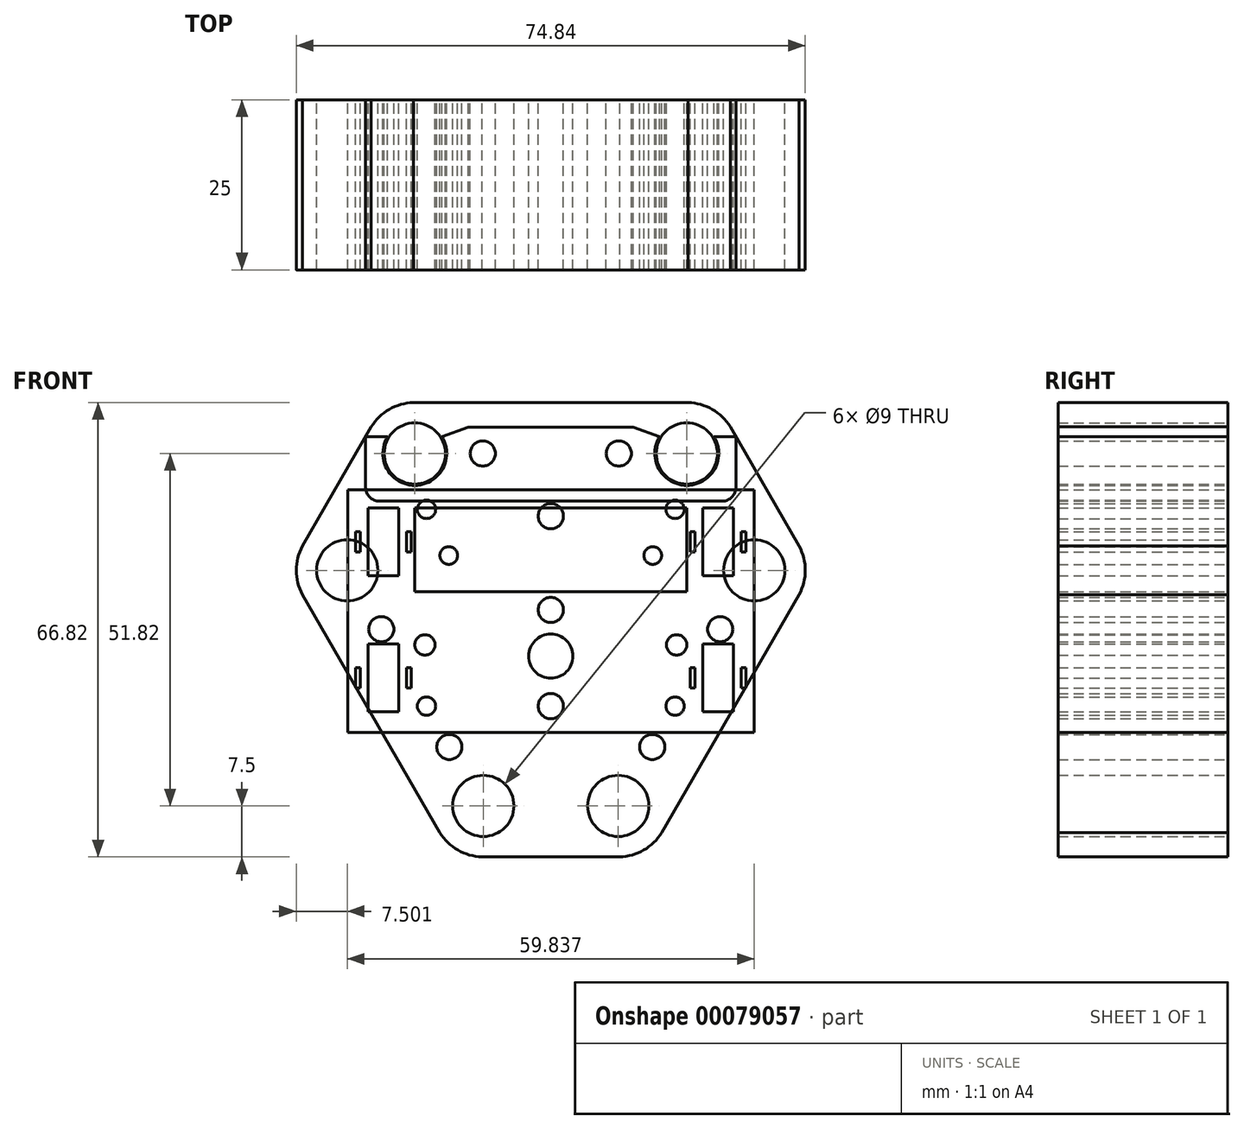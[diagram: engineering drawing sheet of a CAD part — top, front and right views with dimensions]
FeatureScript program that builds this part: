
annotation { "Feature Type Name" : "Feature", "Feature Type Description" : "" }
export const myFeature = defineFeature(function(context is Context, id is Id, definition is map)
    precondition{}
    {
        {
            var Q0;
            Q0=qCreatedBy(makeId("Front.planeOp"),FACE);
            var sketch = newSketch(context, id + "F0", { "sketchPlane" : qUnion([Q0])});
            skLineSegment(sketch, "E0.bottom", {"start": v(29.88, 17.64) * mm, "end": v(-29.88, 17.64) * mm});
            skLineSegment(sketch, "E0.left", {"start": v(29.88, 17.64) * mm, "end": v(29.88, -18) * mm});
            skLineSegment(sketch, "E0.right", {"start": v(-29.88, 17.64) * mm, "end": v(-29.88, -18) * mm});
            skPoint(sketch, "E0.middle", {"position": v(0, 0) * mm});
            skLineSegment(sketch, "E1.bottom", {"start": v(-22.38, 15) * mm, "end": v(-26.88, 15) * mm});
            skLineSegment(sketch, "E1.top", {"start": v(-22.38, 5) * mm, "end": v(-26.88, 5) * mm});
            skLineSegment(sketch, "E1.left", {"start": v(-22.38, 15) * mm, "end": v(-22.38, 5) * mm});
            skLineSegment(sketch, "E1.right", {"start": v(-26.88, 15) * mm, "end": v(-26.88, 5) * mm});
            skPoint(sketch, "E1.middle", {"position": v(-24.63, 10) * mm});
            skLineSegment(sketch, "E2", {"start": v(0, 17.64) * mm, "end": v(0, -17.64) * mm, "construction": true});
            skLineSegment(sketch, "E3", {"start": v(-26.88, 10) * mm, "end": v(-29.88, 10) * mm, "construction": true});
            skLineSegment(sketch, "E4", {"start": v(-24.63, 15) * mm, "end": v(-24.63, 5) * mm, "construction": true});
            skLineSegment(sketch, "E5.bottom", {"start": v(-28.03, 11.5) * mm, "end": v(-28.73, 11.5) * mm});
            skLineSegment(sketch, "E5.top", {"start": v(-28.03, 8.5) * mm, "end": v(-28.73, 8.5) * mm});
            skLineSegment(sketch, "E5.left", {"start": v(-28.03, 11.5) * mm, "end": v(-28.03, 8.5) * mm});
            skLineSegment(sketch, "E5.right", {"start": v(-28.73, 11.5) * mm, "end": v(-28.73, 8.5) * mm});
            skPoint(sketch, "E5.middle", {"position": v(-28.38, 10) * mm});
            skLineSegment(sketch, "E6.MirrorCS", {"start": v(-20.53, 11.5) * mm, "end": v(-20.53, 8.5) * mm});
            skLineSegment(sketch, "E7.MirrorCS", {"start": v(-21.23, 11.5) * mm, "end": v(-20.53, 11.5) * mm});
            skLineSegment(sketch, "E8.MirrorCS", {"start": v(-21.23, 11.5) * mm, "end": v(-21.23, 8.5) * mm});
            skLineSegment(sketch, "E9.MirrorCS", {"start": v(-21.23, 8.5) * mm, "end": v(-20.53, 8.5) * mm});
            skLineSegment(sketch, "E10", {"start": v(-29.88, 0) * mm, "end": v(29.88, 0) * mm, "construction": true});
            skCircle(sketch, "E11", {"center": v(-15, 8) * mm, "radius": 4.64 * mm, "construction": true});
            skCircle(sketch, "E12", {"center": v(0, 13.79) * mm, "radius": 1.85 * mm});
            skLineSegment(sketch, "E13.MirrorCS", {"start": v(-28.03, -11.5) * mm, "end": v(-28.73, -11.5) * mm});
            skLineSegment(sketch, "E14.MirrorCS", {"start": v(-21.23, -8.5) * mm, "end": v(-20.53, -8.5) * mm});
            skLineSegment(sketch, "E15.MirrorCS", {"start": v(-28.03, -8.5) * mm, "end": v(-28.73, -8.5) * mm});
            skLineSegment(sketch, "E16.MirrorCS", {"start": v(-21.23, -11.5) * mm, "end": v(-21.23, -8.5) * mm});
            skLineSegment(sketch, "E17.MirrorCS", {"start": v(-20.53, -11.5) * mm, "end": v(-20.53, -8.5) * mm});
            skLineSegment(sketch, "E18.MirrorCS", {"start": v(-28.73, -11.5) * mm, "end": v(-28.73, -8.5) * mm});
            skLineSegment(sketch, "E19.MirrorCS", {"start": v(-28.03, -11.5) * mm, "end": v(-28.03, -8.5) * mm});
            skLineSegment(sketch, "E20.MirrorCS", {"start": v(-26.88, -10) * mm, "end": v(-29.88, -10) * mm, "construction": true});
            skLineSegment(sketch, "E21.MirrorCS", {"start": v(-21.23, -11.5) * mm, "end": v(-20.53, -11.5) * mm});
            skLineSegment(sketch, "E22.MirrorCS", {"start": v(-22.38, -5) * mm, "end": v(-26.88, -5) * mm});
            skLineSegment(sketch, "E23.MirrorCS", {"start": v(-22.38, -15) * mm, "end": v(-26.88, -15) * mm});
            skPoint(sketch, "E24.MirrorP", {"position": v(-28.38, -10) * mm});
            skLineSegment(sketch, "E25.MirrorCS", {"start": v(-24.63, -15) * mm, "end": v(-24.63, -5) * mm, "construction": true});
            skLineSegment(sketch, "E26.MirrorCS", {"start": v(-26.88, -15) * mm, "end": v(-26.88, -5) * mm});
            skLineSegment(sketch, "E27.MirrorCS", {"start": v(-22.38, -15) * mm, "end": v(-22.38, -5) * mm});
            skPoint(sketch, "E28.MirrorP", {"position": v(-24.63, -10) * mm});
            skLineSegment(sketch, "E29", {"start": v(-29.88, -18) * mm, "end": v(29.88, -18) * mm});
            skPoint(sketch, "E30.orphan", {"position": v(-29.88, -17.64) * mm});
            skPoint(sketch, "E31.orphan", {"position": v(29.88, -17.64) * mm});
            skCircle(sketch, "E32", {"center": v(0, 0) * mm, "radius": 1.85 * mm});
            skCircle(sketch, "E33", {"center": v(0, -14.15) * mm, "radius": 1.85 * mm});
            skCircle(sketch, "E34", {"center": v(-18.28, -14.15) * mm, "radius": 1.35 * mm});
            skCircle(sketch, "E35.MirrorC", {"center": v(18.28, -14.15) * mm, "radius": 1.35 * mm});
            skCircle(sketch, "E36", {"center": v(-18.28, 14.79) * mm, "radius": 1.35 * mm});
            skCircle(sketch, "E37.MirrorC", {"center": v(18.28, 14.79) * mm, "radius": 1.35 * mm});
            skCircle(sketch, "E38.MirrorC", {"center": v(15, 8) * mm, "radius": 4.64 * mm, "construction": true});
            skLineSegment(sketch, "E39.MirrorCS", {"start": v(28.03, -11.5) * mm, "end": v(28.73, -11.5) * mm});
            skLineSegment(sketch, "E40.MirrorCS", {"start": v(28.03, -8.5) * mm, "end": v(28.73, -8.5) * mm});
            skLineSegment(sketch, "E41.MirrorCS", {"start": v(26.88, 10) * mm, "end": v(29.88, 10) * mm, "construction": true});
            skLineSegment(sketch, "E42.MirrorCS", {"start": v(28.03, 11.5) * mm, "end": v(28.73, 11.5) * mm});
            skLineSegment(sketch, "E43.MirrorCS", {"start": v(28.03, -11.5) * mm, "end": v(28.03, -8.5) * mm});
            skLineSegment(sketch, "E44.MirrorCS", {"start": v(22.38, -15) * mm, "end": v(22.38, -5) * mm});
            skLineSegment(sketch, "E45.MirrorCS", {"start": v(21.23, 11.5) * mm, "end": v(21.23, 8.5) * mm});
            skLineSegment(sketch, "E46.MirrorCS", {"start": v(21.23, -11.5) * mm, "end": v(21.23, -8.5) * mm});
            skLineSegment(sketch, "E47.MirrorCS", {"start": v(26.88, -10) * mm, "end": v(29.88, -10) * mm, "construction": true});
            skLineSegment(sketch, "E48.MirrorCS", {"start": v(28.73, -11.5) * mm, "end": v(28.73, -8.5) * mm});
            skLineSegment(sketch, "E49.MirrorCS", {"start": v(26.88, -15) * mm, "end": v(26.88, -5) * mm});
            skLineSegment(sketch, "E50.MirrorCS", {"start": v(20.53, 11.5) * mm, "end": v(20.53, 8.5) * mm});
            skLineSegment(sketch, "E51.MirrorCS", {"start": v(28.73, 11.5) * mm, "end": v(28.73, 8.5) * mm});
            skLineSegment(sketch, "E52.MirrorCS", {"start": v(21.23, 11.5) * mm, "end": v(20.53, 11.5) * mm});
            skLineSegment(sketch, "E53.MirrorCS", {"start": v(21.23, -8.5) * mm, "end": v(20.53, -8.5) * mm});
            skLineSegment(sketch, "E54.MirrorCS", {"start": v(28.03, 8.5) * mm, "end": v(28.73, 8.5) * mm});
            skLineSegment(sketch, "E55.MirrorCS", {"start": v(26.88, 15) * mm, "end": v(26.88, 5) * mm});
            skLineSegment(sketch, "E56.MirrorCS", {"start": v(22.38, 15) * mm, "end": v(22.38, 5) * mm});
            skLineSegment(sketch, "E57.MirrorCS", {"start": v(21.23, -11.5) * mm, "end": v(20.53, -11.5) * mm});
            skLineSegment(sketch, "E58.MirrorCS", {"start": v(28.03, 11.5) * mm, "end": v(28.03, 8.5) * mm});
            skLineSegment(sketch, "E59.MirrorCS", {"start": v(21.23, 8.5) * mm, "end": v(20.53, 8.5) * mm});
            skLineSegment(sketch, "E60.MirrorCS", {"start": v(20.53, -11.5) * mm, "end": v(20.53, -8.5) * mm});
            skLineSegment(sketch, "E61.MirrorCS", {"start": v(22.38, -15) * mm, "end": v(26.88, -15) * mm});
            skLineSegment(sketch, "E62.MirrorCS", {"start": v(22.38, -5) * mm, "end": v(26.88, -5) * mm});
            skLineSegment(sketch, "E63.MirrorCS", {"start": v(22.38, 5) * mm, "end": v(26.88, 5) * mm});
            skLineSegment(sketch, "E64.MirrorCS", {"start": v(22.38, 15) * mm, "end": v(26.88, 15) * mm});
            skPoint(sketch, "E65.MirrorP", {"position": v(24.63, -10) * mm});
            skPoint(sketch, "E66.MirrorP", {"position": v(24.63, 10) * mm});
            skPoint(sketch, "E67.MirrorP", {"position": v(28.38, -10) * mm});
            skPoint(sketch, "E68.MirrorP", {"position": v(28.38, 10) * mm});
            skLineSegment(sketch, "E69.MirrorCS", {"start": v(24.63, 15) * mm, "end": v(24.63, 5) * mm, "construction": true});
            skLineSegment(sketch, "E70.MirrorCS", {"start": v(24.63, -15) * mm, "end": v(24.63, -5) * mm, "construction": true});
            skCircle(sketch, "E71", {"center": v(-15, 8) * mm, "radius": 1.3 * mm});
            skCircle(sketch, "E72", {"center": v(15, 8) * mm, "radius": 1.3 * mm});
            skSolve(sketch);
        }
        {
            var Q0;
            Q0=qCreatedBy(makeId("Front.planeOp"),FACE);
            var sketch = newSketch(context, id + "F1", { "sketchPlane" : qUnion([Q0])});
            skCircle(sketch, "E73", {"center": v(-20, 23) * mm, "radius": 4.5 * mm});
            skLineSegment(sketch, "E74", {"start": v(0, 0) * mm, "end": v(0, 51.03) * mm, "construction": true});
            skCircle(sketch, "E75.MirrorC", {"center": v(20, 23) * mm, "radius": 4.5 * mm});
            skCircle(sketch, "E76.1.0", {"center": v(-9.92, -28.82) * mm, "radius": 4.5 * mm});
            skCircle(sketch, "E76.1.1", {"center": v(-29.92, 5.82) * mm, "radius": 4.5 * mm});
            skCircle(sketch, "E76.2.0", {"center": v(29.92, 5.82) * mm, "radius": 4.5 * mm});
            skCircle(sketch, "E76.2.1", {"center": v(9.92, -28.82) * mm, "radius": 4.5 * mm});
            skPoint(sketch, "E76.center", {"position": v(0, 0) * mm});
            skLineSegment(sketch, "E77", {"start": v(-24.33, 30.5) * mm, "end": v(0, 30.5) * mm});
            skLineSegment(sketch, "E78.MirrorCS", {"start": v(24.33, 30.5) * mm, "end": v(0, 30.5) * mm});
            skLineSegment(sketch, "E79", {"start": v(24.33, 30.5) * mm, "end": v(38.58, 5.82) * mm});
            skLineSegment(sketch, "E80.1.0", {"start": v(-38.58, 5.82) * mm, "end": v(-26.41, -15.25) * mm});
            skLineSegment(sketch, "E80.1.1", {"start": v(-38.58, 5.82) * mm, "end": v(-24.33, 30.5) * mm});
            skLineSegment(sketch, "E80.1.2", {"start": v(-14.25, -36.32) * mm, "end": v(-26.41, -15.25) * mm});
            skLineSegment(sketch, "E80.2.0", {"start": v(14.25, -36.32) * mm, "end": v(26.41, -15.25) * mm});
            skLineSegment(sketch, "E80.2.1", {"start": v(14.25, -36.32) * mm, "end": v(-14.25, -36.32) * mm});
            skLineSegment(sketch, "E80.2.2", {"start": v(38.58, 5.82) * mm, "end": v(26.41, -15.25) * mm});
            skLineSegment(sketch, "E81", {"start": v(-29.92, 5.82) * mm, "end": v(-20, 23) * mm, "construction": true});
            skLineSegment(sketch, "E82", {"start": v(-20, 23) * mm, "end": v(0, 23) * mm, "construction": true});
            skCircle(sketch, "E83", {"center": v(-10, 23) * mm, "radius": 1.85 * mm});
            skCircle(sketch, "E84.MirrorC", {"center": v(10, 23) * mm, "radius": 1.85 * mm});
            skCircle(sketch, "E85.1.0", {"center": v(-14.92, -20.16) * mm, "radius": 1.85 * mm});
            skCircle(sketch, "E85.1.1", {"center": v(-24.92, -2.84) * mm, "radius": 1.85 * mm});
            skCircle(sketch, "E85.2.0", {"center": v(24.92, -2.84) * mm, "radius": 1.85 * mm});
            skCircle(sketch, "E85.2.1", {"center": v(14.92, -20.16) * mm, "radius": 1.85 * mm});
            skLineSegment(sketch, "E86.bottom", {"start": v(8.5, -2.3) * mm, "end": v(-8.5, -2.3) * mm, "construction": true});
            skLineSegment(sketch, "E86.top", {"start": v(8.5, -18.19) * mm, "end": v(-8.5, -18.19) * mm, "construction": true});
            skLineSegment(sketch, "E86.left", {"start": v(8.5, -2.3) * mm, "end": v(8.5, -18.19) * mm, "construction": true});
            skLineSegment(sketch, "E86.right", {"start": v(-8.5, -2.3) * mm, "end": v(-8.5, -18.19) * mm, "construction": true});
            skPoint(sketch, "E86.middle", {"position": v(0, -10.24) * mm});
            skLineSegment(sketch, "E87.bottom", {"start": v(20, 15) * mm, "end": v(-20, 15) * mm});
            skLineSegment(sketch, "E87.top", {"start": v(20, 2.7) * mm, "end": v(-20, 2.7) * mm});
            skLineSegment(sketch, "E87.left", {"start": v(20, 15) * mm, "end": v(20, 2.7) * mm});
            skLineSegment(sketch, "E87.right", {"start": v(-20, 15) * mm, "end": v(-20, 2.7) * mm});
            skPoint(sketch, "E87.middle", {"position": v(0, 8.85) * mm});
            skCircle(sketch, "E88", {"center": v(0, -6.8) * mm, "radius": 3.25 * mm});
            skArc(sketch, "E89", {"start": v(-20.21, 30.5) * mm, "mid": v(-23.75, 29.5) * mm, "end": v(-26.39, 26.94) * mm});
            skArc(sketch, "E90.MirrorCS", {"start": v(20.21, 30.5) * mm, "mid": v(23.75, 29.5) * mm, "end": v(26.39, 26.94) * mm});
            skArc(sketch, "E91.1.0", {"start": v(-16.3, -32.76) * mm, "mid": v(-13.67, -35.32) * mm, "end": v(-10.13, -36.32) * mm});
            skArc(sketch, "E91.1.1", {"start": v(-36.52, 2.26) * mm, "mid": v(-37.42, 5.82) * mm, "end": v(-36.52, 9.38) * mm});
            skArc(sketch, "E91.2.0", {"start": v(36.52, 2.26) * mm, "mid": v(37.42, 5.82) * mm, "end": v(36.52, 9.38) * mm});
            skArc(sketch, "E91.2.1", {"start": v(16.3, -32.76) * mm, "mid": v(13.67, -35.32) * mm, "end": v(10.13, -36.32) * mm});
            skCircle(sketch, "E92", {"center": v(-18.5, -5.15) * mm, "radius": 1.5 * mm});
            skCircle(sketch, "E93.MirrorC", {"center": v(18.5, -5.15) * mm, "radius": 1.5 * mm});
            skSolve(sketch);
        }
        {
            var Q0;
            Q0=qCreatedBy(makeId("Front.planeOp"),FACE);
            var sketch = newSketch(context, id + "F2", { "sketchPlane" : qUnion([Q0])});
            skPoint(sketch, "E94.0", {"position": v(-20, 23) * mm});
            skArc(sketch, "E95", {"start": v(-23.98, 25.5) * mm, "mid": v(-20, 18.3) * mm, "end": v(-16.02, 25.5) * mm});
            skLineSegment(sketch, "E96.0", {"start": v(-38.58, 5.82) * mm, "end": v(-24.33, 30.5) * mm, "construction": true});
            skLineSegment(sketch, "E97", {"start": v(-23.98, 25.5) * mm, "end": v(-27.22, 25.5) * mm});
            skLineSegment(sketch, "E98", {"start": v(-27.22, 25.5) * mm, "end": v(-27.22, 18) * mm});
            skLineSegment(sketch, "E99", {"start": v(-25.22, 16) * mm, "end": v(0, 16) * mm});
            skLineSegment(sketch, "E100", {"start": v(-16.02, 25.5) * mm, "end": v(-12.14, 26.86) * mm});
            skLineSegment(sketch, "E101", {"start": v(-12.14, 26.86) * mm, "end": v(0, 26.86) * mm});
            skLineSegment(sketch, "E102.MirrorCS", {"start": v(12.14, 26.86) * mm, "end": v(0, 26.86) * mm});
            skLineSegment(sketch, "E103.MirrorCS", {"start": v(16.02, 25.5) * mm, "end": v(12.14, 26.86) * mm});
            skArc(sketch, "E104.MirrorC", {"start": v(23.98, 25.5) * mm, "mid": v(20, 18.3) * mm, "end": v(16.02, 25.5) * mm});
            skLineSegment(sketch, "E105.MirrorCS", {"start": v(23.98, 25.5) * mm, "end": v(27.22, 25.5) * mm});
            skLineSegment(sketch, "E106.MirrorCS", {"start": v(27.22, 25.5) * mm, "end": v(27.22, 18) * mm});
            skLineSegment(sketch, "E107.MirrorCS", {"start": v(25.22, 16) * mm, "end": v(0, 16) * mm});
            skCircle(sketch, "E108.0", {"center": v(-10, 23) * mm, "radius": 1.85 * mm});
            skCircle(sketch, "E109.0", {"center": v(10, 23) * mm, "radius": 1.85 * mm});
            skPoint(sketch, "E110.visualSharp", {"position": v(-27.22, 16) * mm});
            skArc(sketch, "E110.filletArc", {"start": v(-27.22, 18) * mm, "mid": v(-26.63, 16.59) * mm, "end": v(-25.22, 16) * mm});
            skPoint(sketch, "E111.visualSharp", {"position": v(27.22, 16) * mm});
            skArc(sketch, "E111.filletArc", {"start": v(25.22, 16) * mm, "mid": v(26.63, 16.59) * mm, "end": v(27.22, 18) * mm});
            skSolve(sketch);
        }
        {
            var Q0;
            Q0=makeQuery(id+"F1.imprint","IMPRINT",FACE,{"disambiguationData":[TD([[makeQuery(id+"F1.imprint","IMPRINT",EDGE,{"derivedFrom":sQuery(id+"F1.wireOp",EDGE,"E73")}),-1.0]])]});
            extrude(context, id + "F3", {"entities" : qUnion([Q0]), "depth" : 25 * mm});
        }
        {
            var Q0;
            Q0=makeQuery(id+"F2.imprint","IMPRINT",FACE,{"disambiguationData":[TD([[makeQuery(id+"F2.imprint","IMPRINT",EDGE,{"derivedFrom":sQuery(id+"F2.wireOp",EDGE,"E95")}),-1.0]])]});
            extrude(context, id + "F4", {"entities" : qUnion([Q0]), "depth" : 25 * mm});
        }
        {
            var Q0;
            Q0=makeQuery(id+"F0.imprint","IMPRINT",FACE,{"disambiguationData":[TD([[makeQuery(id+"F0.imprint","IMPRINT",EDGE,{"derivedFrom":sQuery(id+"F0.wireOp",EDGE,"E0.bottom")}),1.0]])]});
            extrude(context, id + "F5", {"entities" : qUnion([Q0]), "depth" : 25 * mm});
        }
    });
